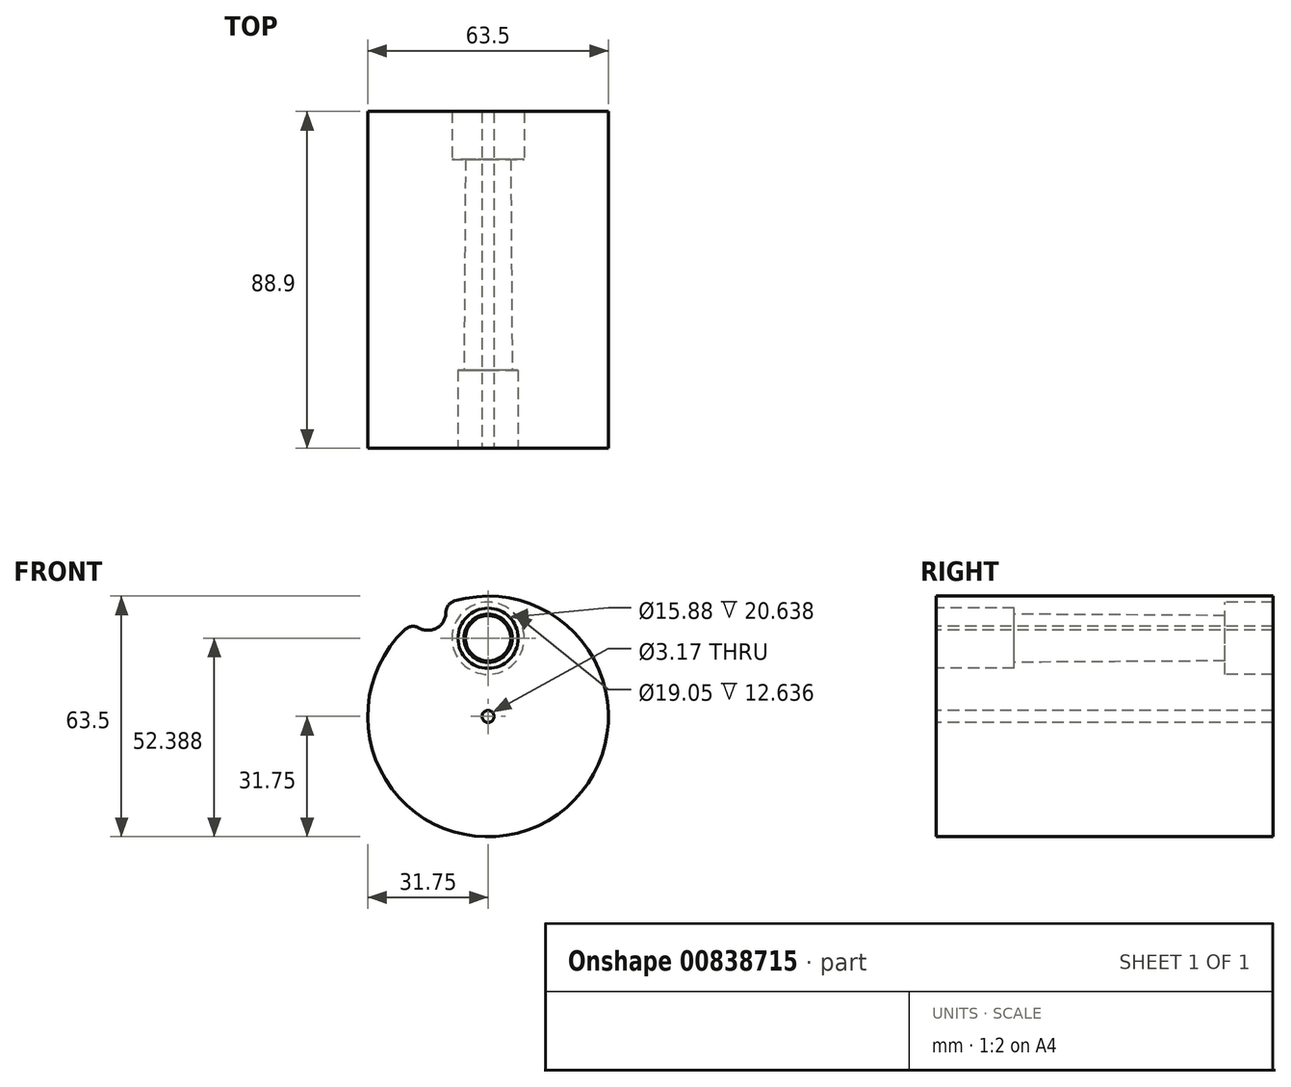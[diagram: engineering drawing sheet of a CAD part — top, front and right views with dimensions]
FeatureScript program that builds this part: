
annotation { "Feature Type Name" : "Feature", "Feature Type Description" : "" }
export const myFeature = defineFeature(function(context is Context, id is Id, definition is map)
    precondition{}
    {
        {
            var Q0;
            Q0=qCreatedBy(makeId("Front.planeOp"),FACE);
            var sketch = newSketch(context, id + "F0", { "sketchPlane" : qUnion([Q0])});
            skCircle(sketch, "E0", {"center": v(0, 0) * mm, "radius": 31.75 * mm});
            skSolve(sketch);
        }
        {
            var Q0;
            Q0 = qSketchRegion(id + "F0", true);
            extrude(context, id + "F1", {"entities" : qUnion([Q0]), "depth" : 88.9 * mm, "offsetDistance" : 25.4 * mm});
        }
        {
            var Q0;
            Q0=makeQuery(id+"F1.opExtrude","CAP_FACE",FACE,{"disambiguationData":[OSD([sQuery(id+"F0.wireOp",EDGE,"E0")])],"isStart":false});
            var sketch = newSketch(context, id + "F2", { "sketchPlane" : qUnion([Q0])});
            skCircle(sketch, "E1", {"center": v(0, 20.64) * mm, "radius": 7.94 * mm});
            skSolve(sketch);
        }
        {
            var Q0;
            Q0 = qSketchRegion(id + "F2", true);
            extrude(context, id + "F3", {"entities" : qUnion([Q0]), "operationType" : NewBodyOperationType.REMOVE, "oppositeDirection" : true, "depth" : 20.64 * mm, "offsetDistance" : 25.4 * mm});
        }
        {
            var Q0;
            Q0=makeQuery(id+"F3.boolean.opBoolean","COPY",FACE,{"derivedFrom":makeQuery(id+"F3.opExtrude","CAP_FACE",FACE,{"disambiguationData":[OSD([sQuery(id+"F2.wireOp",EDGE,"E1")])],"isStart":false})});
            var sketch = newSketch(context, id + "F4", { "sketchPlane" : qUnion([Q0])});
            skCircle(sketch, "E2", {"center": v(0, 20.64) * mm, "radius": 6.35 * mm});
            skSolve(sketch);
        }
        {
            var Q0;
            Q0 = qSketchRegion(id + "F4", true);
            extrude(context, id + "F5", {"entities" : qUnion([Q0]), "operationType" : NewBodyOperationType.REMOVE, "oppositeDirection" : true, "depth" : 55.63 * mm, "offsetDistance" : 25.4 * mm, "hasDraft" : true, "draftAngle" : .375 * degree, "draftPullDirection" : true});
        }
        {
            var Q0;
            Q0=makeQuery(id+"F1.opExtrude","CAP_FACE",FACE,{"disambiguationData":[OSD([sQuery(id+"F0.wireOp",EDGE,"E0")])],"isStart":false});
            var sketch = newSketch(context, id + "F6", { "sketchPlane" : qUnion([Q0])});
            skCircle(sketch, "E3", {"center": v(0, 0) * mm, "radius": 1.59 * mm});
            skSolve(sketch);
        }
        {
            var Q0;
            Q0 = qSketchRegion(id + "F6", true);
            extrude(context, id + "F7", {"entities" : qUnion([Q0]), "operationType" : NewBodyOperationType.REMOVE, "endBound" : BoundingType.THROUGH_ALL, "oppositeDirection" : true, "depth" : 25.4 * mm, "offsetDistance" : 25.4 * mm});
        }
        {
            var Q0;
            Q0=makeQuery(id+"F5.boolean.opBoolean","COPY",FACE,{"derivedFrom":makeQuery(id+"F5.opExtrude","CAP_FACE",FACE,{"disambiguationData":[OSD([sQuery(id+"F4.wireOp",EDGE,"E2")])],"isStart":false})});
            var sketch = newSketch(context, id + "F8", { "sketchPlane" : qUnion([Q0])});
            skCircle(sketch, "E4", {"center": v(0, 20.64) * mm, "radius": 9.53 * mm});
            skSolve(sketch);
        }
        {
            var Q0;
            Q0 = qSketchRegion(id + "F8", true);
            extrude(context, id + "F9", {"entities" : qUnion([Q0]), "operationType" : NewBodyOperationType.REMOVE, "endBound" : BoundingType.THROUGH_ALL, "oppositeDirection" : true, "depth" : 25.4 * mm, "offsetDistance" : 25.4 * mm});
        }
        {
            var Q0;
            Q0=makeQuery(id+"F1.opExtrude","CAP_FACE",FACE,{"disambiguationData":[OSD([sQuery(id+"F0.wireOp",EDGE,"E0")])],"isStart":false});
            var sketch = newSketch(context, id + "F10", { "sketchPlane" : qUnion([Q0])});
            skCircle(sketch, "E5", {"center": v(-15.88, 27.5) * mm, "radius": 4.76 * mm});
            skLineSegment(sketch, "E6", {"start": v(-15.88, 27.5) * mm, "end": v(0, 0) * mm, "construction": true});
            skLineSegment(sketch, "E7", {"start": v(0, 31.75) * mm, "end": v(0, 0) * mm, "construction": true});
            skSolve(sketch);
        }
        {
            var Q0;
            Q0 = qSketchRegion(id + "F10", true);
            extrude(context, id + "F11", {"entities" : qUnion([Q0]), "operationType" : NewBodyOperationType.REMOVE, "endBound" : BoundingType.THROUGH_ALL, "oppositeDirection" : true, "depth" : 25.4 * mm, "offsetDistance" : 25.4 * mm});
        }
        {
            var Q0;
            Q0=makeQuery(id+"F11.boolean.opBoolean","INTERSECT",EDGE,{"disambiguationData":[OD(1.0)],"derivedFrom":[makeQuery(id+"F1.opExtrude","SWEPT_FACE",FACE,{"disambiguationData":[OSD([sQuery(id+"F0.wireOp",EDGE,"E0")])]}),makeQuery(id+"F11.opExtrude","SWEPT_FACE",FACE,{"disambiguationData":[OSD([sQuery(id+"F10.wireOp",EDGE,"E5")])]})]});
            var Q1;
            Q1=makeQuery(id+"F11.boolean.opBoolean","INTERSECT",EDGE,{"disambiguationData":[OD(0.0)],"derivedFrom":[makeQuery(id+"F1.opExtrude","SWEPT_FACE",FACE,{"disambiguationData":[OSD([sQuery(id+"F0.wireOp",EDGE,"E0")])]}),makeQuery(id+"F11.opExtrude","SWEPT_FACE",FACE,{"disambiguationData":[OSD([sQuery(id+"F10.wireOp",EDGE,"E5")])]})]});
            fillet(context, id + "F12", {"entities" : qUnion([Q0, Q1]), "radius" : 3.17 * mm, "tangentPropagation" : true, "allowEdgeOverflow" : false});
        }
    });
